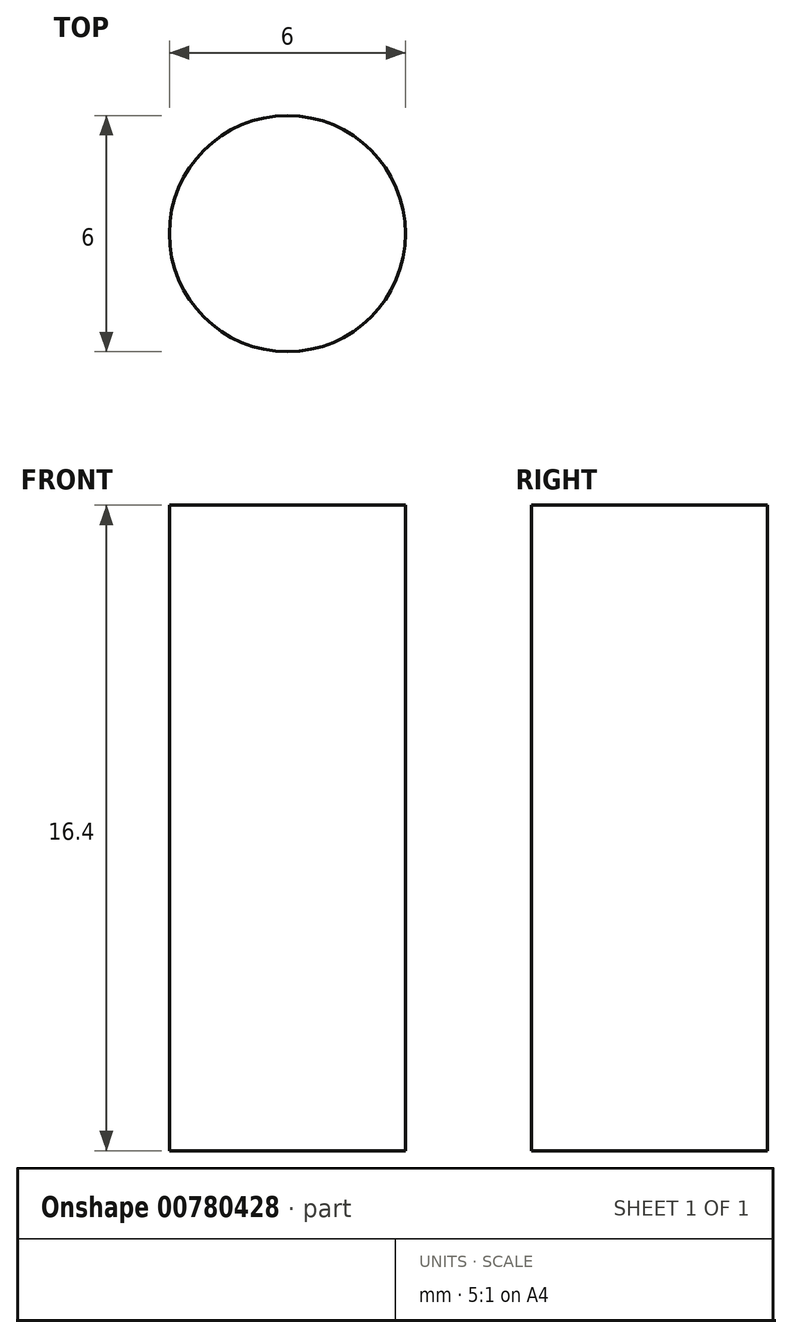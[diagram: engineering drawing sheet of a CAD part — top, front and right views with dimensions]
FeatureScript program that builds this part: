
annotation { "Feature Type Name" : "Feature", "Feature Type Description" : "" }
export const myFeature = defineFeature(function(context is Context, id is Id, definition is map)
    precondition{}
    {
        {
            var Q0;
            Q0=qCreatedBy(makeId("Top.planeOp"),FACE);
            var sketch = newSketch(context, id + "F0", { "sketchPlane" : qUnion([Q0])});
            skCircle(sketch, "E0", {"center": v(0, 0) * mm, "radius": 3 * mm});
            skSolve(sketch);
        }
        {
            var Q0;
            Q0 = qSketchRegion(id + "F0", true);
            extrude(context, id + "F1", {"entities" : qUnion([Q0]), "depth" : 16.4 * mm, "offsetDistance" : 25 * mm});
        }
    });
